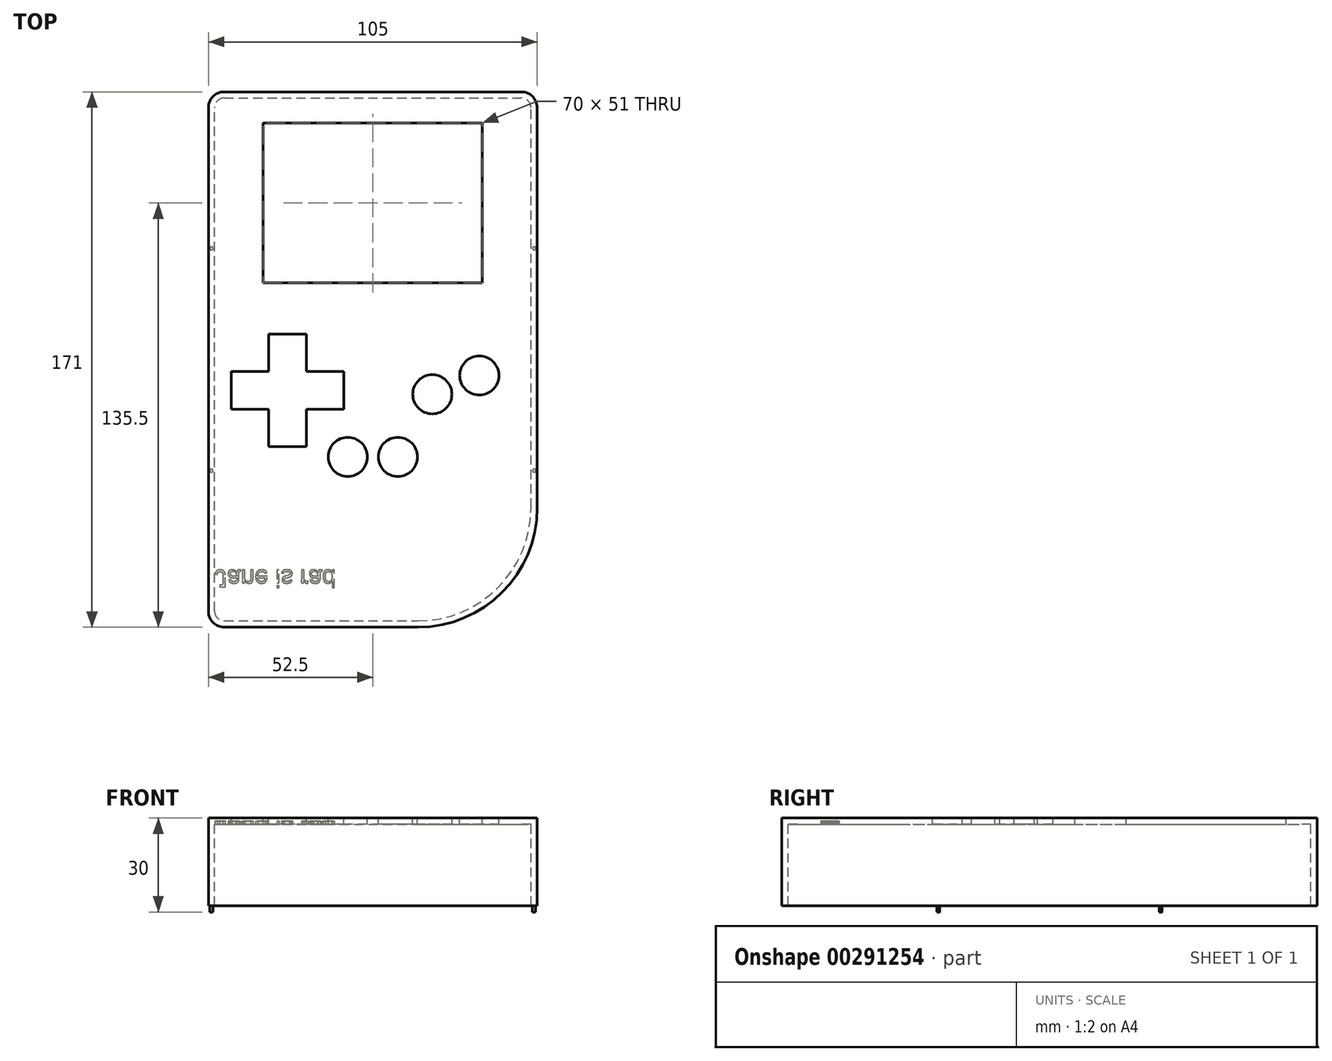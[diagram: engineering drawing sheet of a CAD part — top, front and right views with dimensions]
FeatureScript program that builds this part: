
annotation { "Feature Type Name" : "Feature", "Feature Type Description" : "" }
export const myFeature = defineFeature(function(context is Context, id is Id, definition is map)
    precondition{}
    {
        {
            var Q0;
            Q0=qCreatedBy(makeId("Top.planeOp"),FACE);
            var sketch = newSketch(context, id + "F0", { "sketchPlane" : qUnion([Q0])});
            skLineSegment(sketch, "E0.bottom", {"start": v(0, 0) * mm, "end": v(105, 0) * mm});
            skLineSegment(sketch, "E0.top", {"start": v(0, 171) * mm, "end": v(105, 171) * mm});
            skLineSegment(sketch, "E0.left", {"start": v(0, 0) * mm, "end": v(0, 171) * mm});
            skLineSegment(sketch, "E0.right", {"start": v(105, 0) * mm, "end": v(105, 171) * mm});
            skSolve(sketch);
        }
        {
            var Q0;
            Q0=makeQuery(id+"F0.imprint","IMPRINT",FACE,{"disambiguationData":[TD([[makeQuery(id+"F0.imprint","IMPRINT",EDGE,{"derivedFrom":sQuery(id+"F0.wireOp",EDGE,"E0.bottom")}),1.0]])]});
            extrude(context, id + "F1", {"entities" : qUnion([Q0]), "depth" : 28 * mm});
        }
        {
            var Q0;
            Q0=makeQuery(id+"F1.opExtrude","CAP_FACE",FACE,{"disambiguationData":[OSD([sQuery(id+"F0.wireOp",EDGE,"E0.bottom"),sQuery(id+"F0.wireOp",EDGE,"E0.top"),sQuery(id+"F0.wireOp",EDGE,"E0.left"),sQuery(id+"F0.wireOp",EDGE,"E0.right")])],"isStart":false});
            var sketch = newSketch(context, id + "F2", { "sketchPlane" : qUnion([Q0])});
            skLineSegment(sketch, "E1", {"start": v(52.5, 171) * mm, "end": v(52.5, 0) * mm, "construction": true});
            skLineSegment(sketch, "E2", {"start": v(25.09, 171) * mm, "end": v(25.09, 161) * mm, "construction": true});
            skLineSegment(sketch, "E3.bottom", {"start": v(17.5, 161) * mm, "end": v(87.5, 161) * mm});
            skLineSegment(sketch, "E3.top", {"start": v(17.5, 110) * mm, "end": v(87.5, 110) * mm});
            skLineSegment(sketch, "E3.left", {"start": v(17.5, 161) * mm, "end": v(17.5, 110) * mm});
            skLineSegment(sketch, "E3.right", {"start": v(87.5, 161) * mm, "end": v(87.5, 110) * mm});
            skLineSegment(sketch, "E4", {"start": v(0, 144.67) * mm, "end": v(17.5, 144.67) * mm, "construction": true});
            skLineSegment(sketch, "E5", {"start": v(87.5, 135.5) * mm, "end": v(105, 135.5) * mm, "construction": true});
            skLineSegment(sketch, "E6.bottom", {"start": v(7.25, 93.64) * mm, "end": v(43.25, 93.64) * mm, "construction": true});
            skLineSegment(sketch, "E6.top", {"start": v(7.25, 57.64) * mm, "end": v(43.25, 57.64) * mm, "construction": true});
            skLineSegment(sketch, "E6.left", {"start": v(7.25, 93.64) * mm, "end": v(7.25, 57.64) * mm, "construction": true});
            skLineSegment(sketch, "E6.right", {"start": v(43.25, 93.64) * mm, "end": v(43.25, 57.64) * mm, "construction": true});
            skLineSegment(sketch, "E7", {"start": v(7.25, 81.64) * mm, "end": v(19.25, 81.64) * mm});
            skLineSegment(sketch, "E8", {"start": v(19.25, 81.64) * mm, "end": v(19.25, 93.64) * mm});
            skLineSegment(sketch, "E9", {"start": v(31.25, 93.64) * mm, "end": v(31.25, 81.64) * mm});
            skLineSegment(sketch, "E10", {"start": v(31.25, 81.64) * mm, "end": v(43.25, 81.64) * mm});
            skLineSegment(sketch, "E11", {"start": v(43.25, 69.64) * mm, "end": v(31.25, 69.64) * mm});
            skLineSegment(sketch, "E12", {"start": v(31.25, 69.64) * mm, "end": v(31.25, 57.64) * mm});
            skLineSegment(sketch, "E13", {"start": v(7.25, 69.64) * mm, "end": v(19.25, 69.64) * mm});
            skLineSegment(sketch, "E14", {"start": v(19.25, 69.64) * mm, "end": v(19.25, 57.64) * mm});
            skCircle(sketch, "E15", {"center": v(86.5, 80.39) * mm, "radius": 6.25 * mm});
            skCircle(sketch, "E16", {"center": v(71.5, 74.39) * mm, "radius": 6.25 * mm});
            skCircle(sketch, "E17", {"center": v(44.5, 54.39) * mm, "radius": 6.25 * mm});
            skCircle(sketch, "E18", {"center": v(60.5, 54.39) * mm, "radius": 6.25 * mm});
            skLineSegment(sketch, "E19", {"start": v(44.5, 54.39) * mm, "end": v(0, 54.39) * mm, "construction": true});
            skLineSegment(sketch, "E20", {"start": v(60.5, 54.39) * mm, "end": v(105, 54.39) * mm, "construction": true});
            skLineSegment(sketch, "E21", {"start": v(19.25, 93.64) * mm, "end": v(31.25, 93.64) * mm});
            skLineSegment(sketch, "E22", {"start": v(43.25, 81.64) * mm, "end": v(43.25, 69.64) * mm});
            skLineSegment(sketch, "E23", {"start": v(31.25, 57.64) * mm, "end": v(19.25, 57.64) * mm});
            skLineSegment(sketch, "E24", {"start": v(7.25, 69.64) * mm, "end": v(7.25, 81.64) * mm});
            skLineSegment(sketch, "E25", {"start": v(65.25, 74.39) * mm, "end": v(43.25, 74.39) * mm, "construction": true});
            skLineSegment(sketch, "E26", {"start": v(71.5, 74.39) * mm, "end": v(65.25, 74.39) * mm, "construction": true});
            skLineSegment(sketch, "E27", {"start": v(60.5, 54.39) * mm, "end": v(60.5, 48.14) * mm, "construction": true});
            skLineSegment(sketch, "E28", {"start": v(60.5, 48.14) * mm, "end": v(71.5, 48.14) * mm, "construction": true});
            skLineSegment(sketch, "E29", {"start": v(71.5, 74.39) * mm, "end": v(71.5, 68.14) * mm, "construction": true});
            skLineSegment(sketch, "E30", {"start": v(71.5, 68.14) * mm, "end": v(71.5, 48.14) * mm, "construction": true});
            skLineSegment(sketch, "E31", {"start": v(44.5, 54.39) * mm, "end": v(38.25, 54.39) * mm, "construction": true});
            skSolve(sketch);
        }
        {
            var Q0;
            Q0=makeQuery(id+"F1.opExtrude","SWEPT_EDGE",EDGE,{"disambiguationData":[OSD([sQuery(id+"F0.wireOp",EDGE,"E0.bottom"),sQuery(id+"F0.wireOp",EDGE,"E0.right")])]});
            fillet(context, id + "F3", {"entities" : qUnion([Q0]), "radius" : 38.1 * mm, "tangentPropagation" : true, "allowEdgeOverflow" : false});
        }
        {
            var Q0;
            Q0=makeQuery(id+"F1.opExtrude","SWEPT_EDGE",EDGE,{"disambiguationData":[OSD([sQuery(id+"F0.wireOp",EDGE,"E0.bottom"),sQuery(id+"F0.wireOp",EDGE,"E0.left")])]});
            var Q1;
            Q1=makeQuery(id+"F1.opExtrude","SWEPT_EDGE",EDGE,{"disambiguationData":[OSD([sQuery(id+"F0.wireOp",EDGE,"E0.top"),sQuery(id+"F0.wireOp",EDGE,"E0.left")])]});
            var Q2;
            Q2=makeQuery(id+"F1.opExtrude","SWEPT_EDGE",EDGE,{"disambiguationData":[OSD([sQuery(id+"F0.wireOp",EDGE,"E0.top"),sQuery(id+"F0.wireOp",EDGE,"E0.right")])]});
            fillet(context, id + "F4", {"entities" : qUnion([Q0, Q1, Q2]), "radius" : 5.08 * mm, "tangentPropagation" : true, "allowEdgeOverflow" : false});
        }
        {
            var Q0;
            Q0=makeQuery(id+"F1.opExtrude","CAP_FACE",FACE,{"disambiguationData":[OSD([sQuery(id+"F0.wireOp",EDGE,"E0.bottom"),sQuery(id+"F0.wireOp",EDGE,"E0.top"),sQuery(id+"F0.wireOp",EDGE,"E0.left"),sQuery(id+"F0.wireOp",EDGE,"E0.right")])],"isStart":true});
            shell(context, id + "F5", {"entities" : qUnion([Q0]), "thickness" : 2 * mm});
        }
        {
            var Q0;
            Q0 = qSketchRegion(id + "F2", true);
            extrude(context, id + "F6", {"entities" : qUnion([Q0]), "operationType" : NewBodyOperationType.REMOVE, "endBound" : BoundingType.UP_TO_NEXT, "oppositeDirection" : true, "depth" : 25.4 * mm});
        }
        {
            var Q0;
            Q0=makeQuery(id+"F5.opShell","OFFSET_FACE",FACE,{"disambiguationData":[OSD([sQuery(id+"F0.wireOp",EDGE,"E0.bottom"),sQuery(id+"F0.wireOp",EDGE,"E0.top"),sQuery(id+"F0.wireOp",EDGE,"E0.left"),sQuery(id+"F0.wireOp",EDGE,"E0.right")])]});
            var sketch = newSketch(context, id + "F7", { "sketchPlane" : qUnion([Q0])});
            skText(sketch, "E32", { "text": "Jane is rad", "fontName": "Arimo-Regular.ttf"});
            skPoint(sketch, "E33", {"position": v(92.43, -12.57) * mm});
            const initialGuessF7  = {"E32": [0.002, -0.01827, 1, 0, 0.0057]};
            skSetInitialGuess(sketch, initialGuessF7);
            skSolve(sketch);
        }
        {
            var Q0;
            Q0 = qSketchRegion(id + "F7", true);
            extrude(context, id + "F8", {"entities" : qUnion([Q0]), "operationType" : NewBodyOperationType.REMOVE, "oppositeDirection" : true, "depth" : 1 * mm});
        }
        {
            var Q0;
            Q0=makeQuery(id+"F0.imprint","IMPRINT",FACE,{"disambiguationData":[TD([[makeQuery(id+"F0.imprint","IMPRINT",EDGE,{"derivedFrom":sQuery(id+"F0.wireOp",EDGE,"E0.bottom")}),1.0]])]});
            var sketch = newSketch(context, id + "F9", { "sketchPlane" : qUnion([Q0])});
            skLineSegment(sketch, "E34.bottom", {"start": v(105, 171) * mm, "end": v(0, 171) * mm, "construction": true});
            skLineSegment(sketch, "E34.top", {"start": v(105, 0) * mm, "end": v(0, 0) * mm, "construction": true});
            skLineSegment(sketch, "E34.left", {"start": v(105, 171) * mm, "end": v(105, 0) * mm, "construction": true});
            skLineSegment(sketch, "E34.right", {"start": v(0, 171) * mm, "end": v(0, 0) * mm, "construction": true});
            skLineSegment(sketch, "E35", {"start": v(104, 171) * mm, "end": v(104, 121) * mm, "construction": true});
            skLineSegment(sketch, "E36", {"start": v(1, 171) * mm, "end": v(1, 121) * mm, "construction": true});
            skLineSegment(sketch, "E37", {"start": v(104, 0) * mm, "end": v(104, 50) * mm, "construction": true});
            skLineSegment(sketch, "E38", {"start": v(1, 0) * mm, "end": v(1, 50) * mm, "construction": true});
            skLineSegment(sketch, "E39", {"start": v(105, 159.53) * mm, "end": v(104, 159.53) * mm, "construction": true});
            skLineSegment(sketch, "E40", {"start": v(0, 155.67) * mm, "end": v(1, 155.67) * mm, "construction": true});
            skLineSegment(sketch, "E41", {"start": v(0, 31.8) * mm, "end": v(1, 31.8) * mm, "construction": true});
            skLineSegment(sketch, "E42", {"start": v(105, 37.66) * mm, "end": v(104, 37.66) * mm});
            skCircle(sketch, "E43", {"center": v(104, 50) * mm, "radius": 0.5 * mm});
            skCircle(sketch, "E44", {"center": v(1, 50) * mm, "radius": 0.5 * mm});
            skCircle(sketch, "E45", {"center": v(1, 121) * mm, "radius": 0.5 * mm});
            skCircle(sketch, "E46", {"center": v(104, 121) * mm, "radius": 0.5 * mm});
            skSolve(sketch);
        }
        {
            var Q0;
            Q0 = qSketchRegion(id + "F9", true);
            extrude(context, id + "F10", {"entities" : qUnion([Q0]), "operationType" : NewBodyOperationType.ADD, "oppositeDirection" : true, "depth" : 2 * mm});
        }
    });
